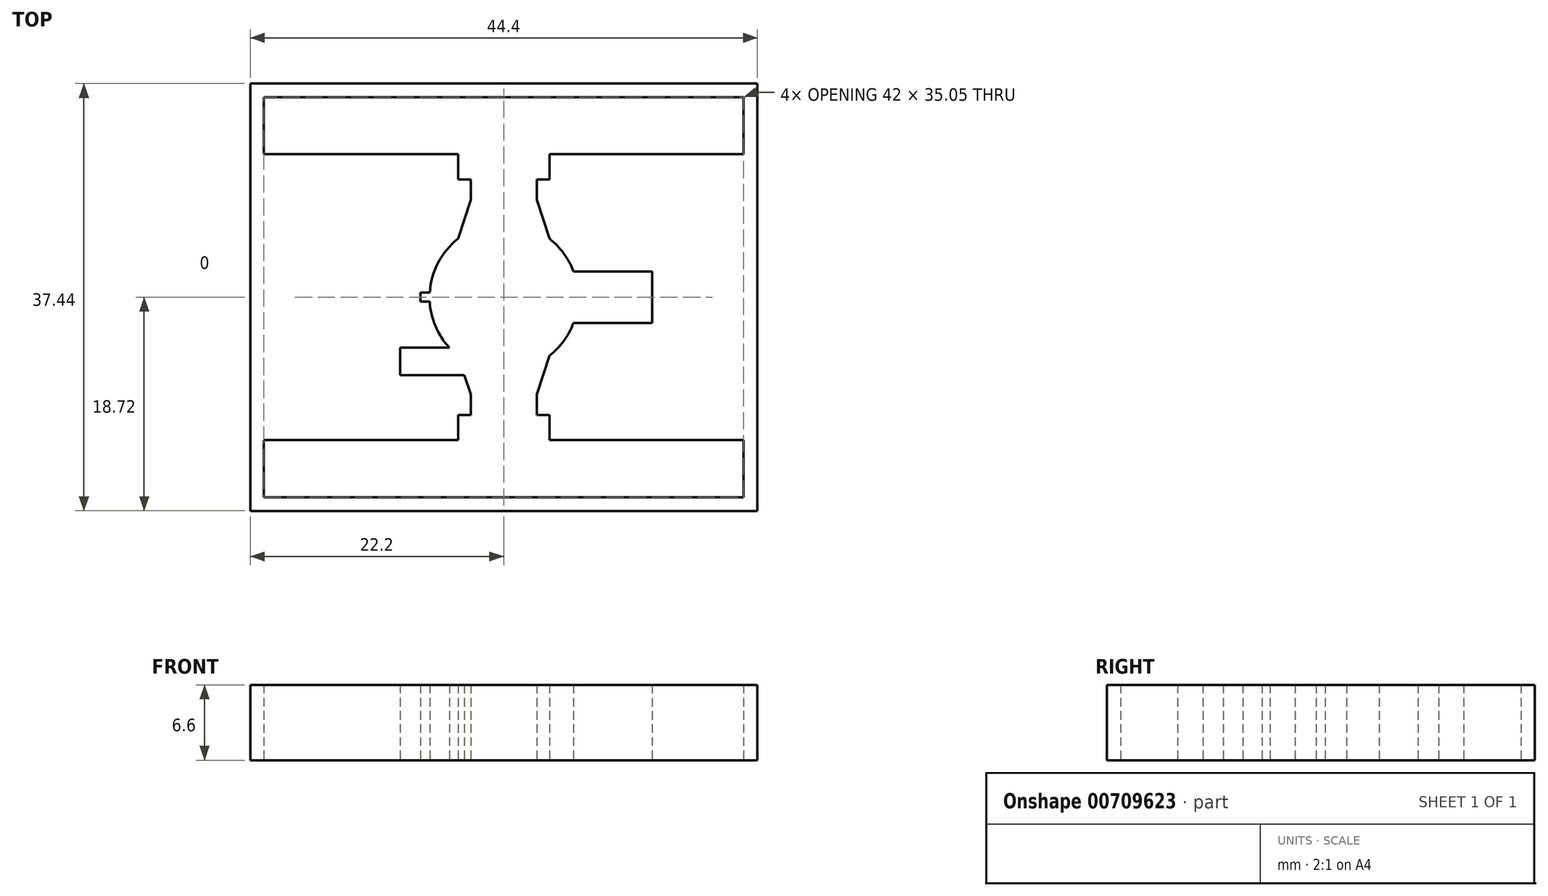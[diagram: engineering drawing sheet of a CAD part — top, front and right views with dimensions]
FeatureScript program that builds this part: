
annotation { "Feature Type Name" : "Feature", "Feature Type Description" : "" }
export const myFeature = defineFeature(function(context is Context, id is Id, definition is map)
    precondition{}
    {
        {
            var Q0;
            Q0=qCreatedBy(makeId("Top.planeOp"),FACE);
            var sketch = newSketch(context, id + "F0", { "sketchPlane" : qUnion([Q0])});
            skArc(sketch, "E0", {"start": v(4, -5.12) * mm, "mid": v(5.25, -3.83) * mm, "end": v(6.1, -2.25) * mm});
            skLineSegment(sketch, "E1.bottom", {"start": v(-21, 12.52) * mm, "end": v(-4, 12.52) * mm});
            skLineSegment(sketch, "E1.left", {"start": v(-21, 12.52) * mm, "end": v(-21, 17.52) * mm});
            skLineSegment(sketch, "E1.right", {"start": v(21, 12.52) * mm, "end": v(21, 17.52) * mm});
            skLineSegment(sketch, "E2.left", {"start": v(-2.9, 8.52) * mm, "end": v(-2.9, 10.32) * mm});
            skLineSegment(sketch, "E3", {"start": v(-2.9, 8.52) * mm, "end": v(-4, 8.52) * mm, "construction": true});
            skLineSegment(sketch, "E4", {"start": v(-4, 8.52) * mm, "end": v(-4, 5.12) * mm, "construction": true});
            skLineSegment(sketch, "E5", {"start": v(-4, 5.12) * mm, "end": v(-2.9, 8.52) * mm});
            skLineSegment(sketch, "E6", {"start": v(-21, 17.52) * mm, "end": v(0, 17.52) * mm});
            skLineSegment(sketch, "E7.MirrorCS", {"start": v(4, 8.52) * mm, "end": v(4, 5.12) * mm, "construction": true});
            skLineSegment(sketch, "E8.MirrorCS", {"start": v(2.9, 8.52) * mm, "end": v(4, 8.52) * mm, "construction": true});
            skLineSegment(sketch, "E9.MirrorCS", {"start": v(4, 5.12) * mm, "end": v(2.9, 8.52) * mm});
            skLineSegment(sketch, "E10.MirrorCS", {"start": v(21, 12.52) * mm, "end": v(4, 12.52) * mm});
            skLineSegment(sketch, "E11.MirrorCS", {"start": v(2.9, 8.52) * mm, "end": v(2.9, 10.32) * mm});
            skLineSegment(sketch, "E12.MirrorCS", {"start": v(4, 10.52) * mm, "end": v(4, 12.52) * mm});
            skLineSegment(sketch, "E13.MirrorCS", {"start": v(21, 17.52) * mm, "end": v(0, 17.52) * mm});
            skLineSegment(sketch, "E14", {"start": v(-29.44, 0) * mm, "end": v(-7.3, 0) * mm, "construction": true});
            skLineSegment(sketch, "E15.MirrorCS", {"start": v(-2.9, -8.52) * mm, "end": v(-4, -8.52) * mm, "construction": true});
            skLineSegment(sketch, "E16.MirrorCS", {"start": v(2.9, -8.52) * mm, "end": v(4, -8.52) * mm, "construction": true});
            skLineSegment(sketch, "E17.MirrorCS", {"start": v(2.9, -8.52) * mm, "end": v(2.9, -10.32) * mm});
            skLineSegment(sketch, "E18.MirrorCS", {"start": v(21, -12.52) * mm, "end": v(21, -17.52) * mm});
            skLineSegment(sketch, "E19.MirrorCS", {"start": v(-4, -8.52) * mm, "end": v(-4, -5.12) * mm, "construction": true});
            skLineSegment(sketch, "E20.MirrorCS", {"start": v(-3.45, -6.82) * mm, "end": v(-2.9, -8.52) * mm});
            skLineSegment(sketch, "E21.MirrorCS", {"start": v(4, -8.52) * mm, "end": v(4, -5.12) * mm, "construction": true});
            skLineSegment(sketch, "E22.MirrorCS", {"start": v(0, 33.28) * mm, "end": v(0, -32.9) * mm, "construction": true});
            skLineSegment(sketch, "E23.MirrorCS", {"start": v(4, -5.12) * mm, "end": v(2.9, -8.52) * mm});
            skLineSegment(sketch, "E24.MirrorCS", {"start": v(-21, -17.52) * mm, "end": v(0, -17.52) * mm});
            skLineSegment(sketch, "E25.MirrorCS", {"start": v(-21, -12.52) * mm, "end": v(-21, -17.52) * mm});
            skArc(sketch, "E26.MirrorC", {"start": v(-4.76, -4.42) * mm, "mid": v(-5.97, -2.56) * mm, "end": v(-6.49, -0.4) * mm});
            skLineSegment(sketch, "E27.MirrorCS", {"start": v(-21, -12.52) * mm, "end": v(-4, -12.52) * mm});
            skLineSegment(sketch, "E28.MirrorCS", {"start": v(21, -17.52) * mm, "end": v(0, -17.52) * mm});
            skLineSegment(sketch, "E29.MirrorCS", {"start": v(21, -12.52) * mm, "end": v(4, -12.52) * mm});
            skPoint(sketch, "E30", {"position": v(-4, -6.82) * mm});
            skLineSegment(sketch, "E31", {"start": v(-3.45, -6.82) * mm, "end": v(-9.06, -6.82) * mm});
            skPoint(sketch, "E32.orphan", {"position": v(-2.5, -6.82) * mm});
            skLineSegment(sketch, "E33", {"start": v(-7.73, -6.82) * mm, "end": v(-7.73, -4.42) * mm, "construction": true});
            skLineSegment(sketch, "E34", {"start": v(-4.76, -4.42) * mm, "end": v(-9.06, -4.42) * mm});
            skLineSegment(sketch, "E35", {"start": v(-9.06, -4.42) * mm, "end": v(-9.06, -6.82) * mm});
            skPoint(sketch, "E36.orphan", {"position": v(-10.73, -6.82) * mm});
            skArc(sketch, "E37.trimOffspring", {"start": v(-4, 5.12) * mm, "mid": v(-5.75, 3.03) * mm, "end": v(-6.49, 0.4) * mm});
            skArc(sketch, "E38.trimOffspring", {"start": v(4, 5.12) * mm, "mid": v(5.25, 3.83) * mm, "end": v(6.1, 2.25) * mm});
            skLineSegment(sketch, "E39.bottom", {"start": v(-22.2, 18.72) * mm, "end": v(22.2, 18.72) * mm});
            skLineSegment(sketch, "E39.top", {"start": v(-22.2, -18.72) * mm, "end": v(22.2, -18.72) * mm});
            skLineSegment(sketch, "E39.left", {"start": v(-22.2, 18.72) * mm, "end": v(-22.2, -18.72) * mm});
            skLineSegment(sketch, "E39.right", {"start": v(22.2, 18.72) * mm, "end": v(22.2, -18.72) * mm});
            skLineSegment(sketch, "E40", {"start": v(-4, 12.52) * mm, "end": v(-4, 10.32) * mm});
            skLineSegment(sketch, "E41", {"start": v(-4, 10.32) * mm, "end": v(-2.9, 10.32) * mm});
            skLineSegment(sketch, "E42.MirrorCS", {"start": v(4, 12.52) * mm, "end": v(4, 10.32) * mm});
            skLineSegment(sketch, "E43.MirrorCS", {"start": v(4, 10.32) * mm, "end": v(2.9, 10.32) * mm});
            skLineSegment(sketch, "E44.MirrorCS", {"start": v(-4, -12.52) * mm, "end": v(-4, -10.32) * mm});
            skLineSegment(sketch, "E45.MirrorCS", {"start": v(-4, -10.32) * mm, "end": v(-2.9, -10.32) * mm});
            skLineSegment(sketch, "E46.MirrorCS", {"start": v(4, -12.52) * mm, "end": v(4, -10.32) * mm});
            skLineSegment(sketch, "E47.MirrorCS", {"start": v(4, -10.32) * mm, "end": v(2.9, -10.32) * mm});
            skLineSegment(sketch, "E48", {"start": v(-2.9, -10.32) * mm, "end": v(-2.9, -8.52) * mm});
            skLineSegment(sketch, "E49", {"start": v(0, 0) * mm, "end": v(13, 0) * mm, "construction": true});
            skLineSegment(sketch, "E50", {"start": v(13, -2.25) * mm, "end": v(13, 2.25) * mm});
            skLineSegment(sketch, "E51", {"start": v(13, -2.25) * mm, "end": v(6.1, -2.25) * mm});
            skLineSegment(sketch, "E52", {"start": v(13, 2.25) * mm, "end": v(6.1, 2.25) * mm});
            skArc(sketch, "E53.trimOffspring", {"start": v(6.1, -2.25) * mm, "mid": v(5.25, -3.83) * mm, "end": v(4, -5.12) * mm});
            skLineSegment(sketch, "E54", {"start": v(-6.5, 0) * mm, "end": v(-7.3, 0) * mm});
            skLineSegment(sketch, "E55", {"start": v(-7.3, 0) * mm, "end": v(-7.3, 0.4) * mm});
            skLineSegment(sketch, "E56", {"start": v(-7.3, 0.4) * mm, "end": v(-6.49, 0.4) * mm});
            skLineSegment(sketch, "E57", {"start": v(-7.3, 0) * mm, "end": v(-7.3, -0.4) * mm});
            skLineSegment(sketch, "E58", {"start": v(-7.3, -0.4) * mm, "end": v(-6.49, -0.4) * mm});
            skLineSegment(sketch, "E59.trimOffspring", {"start": v(-6.5, 0) * mm, "end": v(27.69, 0) * mm, "construction": true});
            skArc(sketch, "E60.trimOffspring", {"start": v(-6.49, 0.4) * mm, "mid": v(-5.75, 3.03) * mm, "end": v(-4, 5.12) * mm});
            skArc(sketch, "E61.trimOffspring", {"start": v(-6.49, -0.4) * mm, "mid": v(-5.97, -2.56) * mm, "end": v(-4.76, -4.42) * mm});
            skSolve(sketch);
        }
        {
            var Q0;
            Q0=makeQuery(id+"F0.imprint","IMPRINT",FACE,{"disambiguationData":[TD([[makeQuery(id+"F0.imprint","IMPRINT",EDGE,{"derivedFrom":sQuery(id+"F0.wireOp",EDGE,"E1.bottom")}),-1.0]])]});
            extrude(context, id + "F1", {"entities" : qUnion([Q0]), "depth" : 6.6 * mm, "offsetDistance" : 25 * mm});
        }
    });
